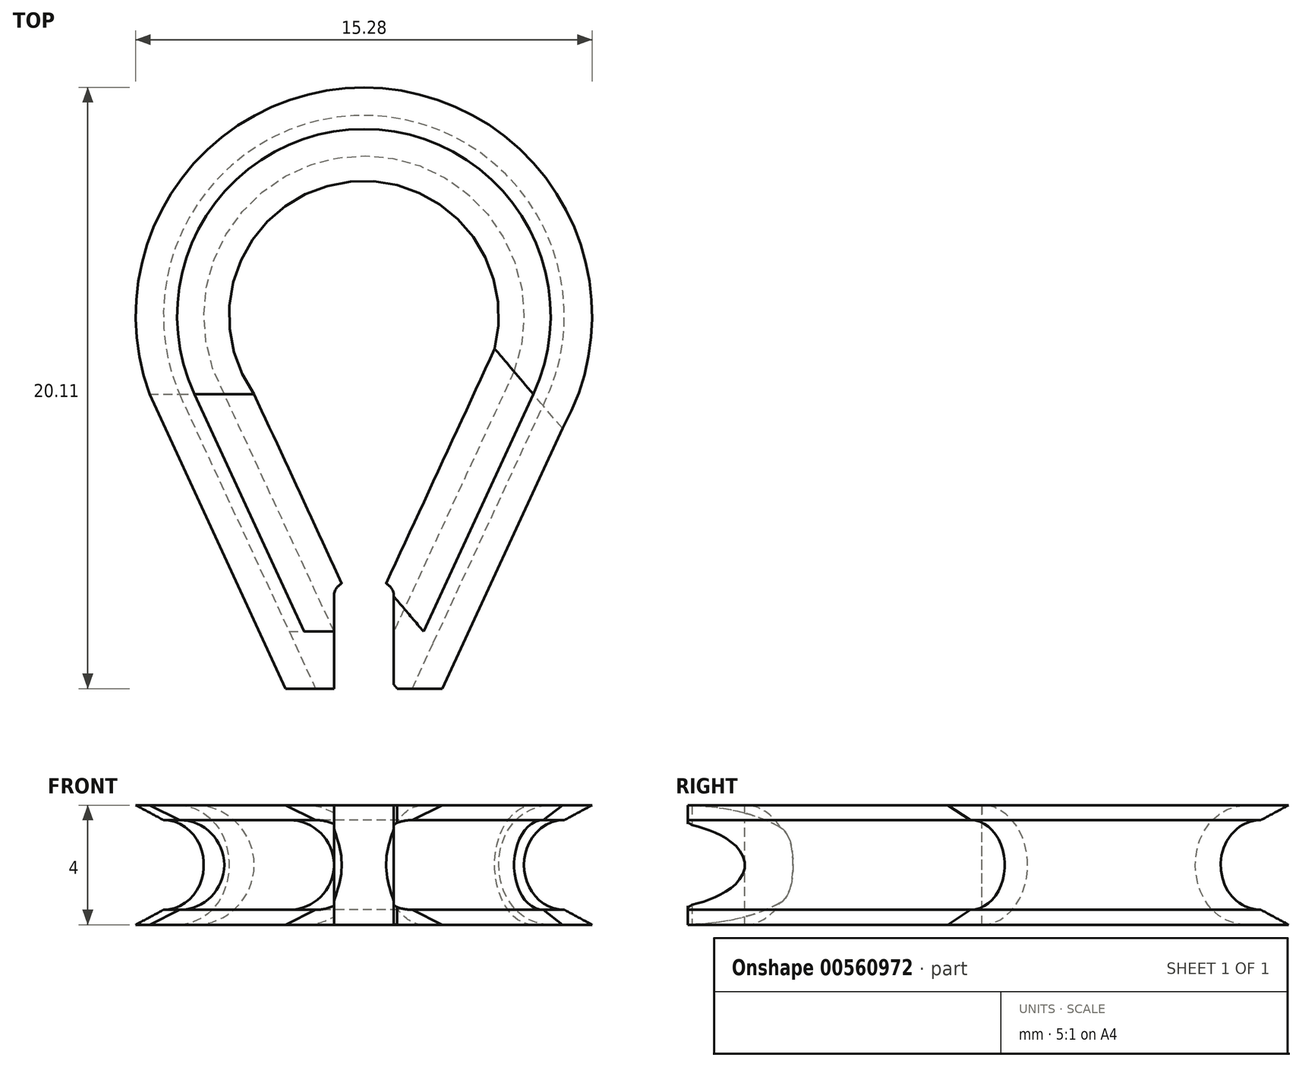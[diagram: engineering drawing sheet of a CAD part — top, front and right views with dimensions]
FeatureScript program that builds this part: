
annotation { "Feature Type Name" : "Feature", "Feature Type Description" : "" }
export const myFeature = defineFeature(function(context is Context, id is Id, definition is map)
    precondition{}
    {
        {
            var Q0;
            Q0=qCreatedBy(makeId("Top.planeOp"),FACE);
            var sketch = newSketch(context, id + "F0", { "sketchPlane" : qUnion([Q0])});
            skArc(sketch, "E0", {"start": v(5.67, -2.62) * mm, "mid": v(0, 6.25) * mm, "end": v(-5.67, -2.62) * mm});
            skLineSegment(sketch, "E1", {"start": v(-5.67, -2.62) * mm, "end": v(-2, -10.56) * mm});
            skLineSegment(sketch, "E2", {"start": v(5.67, -2.62) * mm, "end": v(2, -10.56) * mm});
            skLineSegment(sketch, "E3", {"start": v(2, -10.56) * mm, "end": v(1.12, -12.47) * mm});
            skLineSegment(sketch, "E4", {"start": v(-2, -10.56) * mm, "end": v(-1.12, -12.47) * mm});
            skSolve(sketch);
        }
        {
            var Q0;
            Q0=qCreatedBy(makeId("Front.planeOp"),FACE);
            cPlane(context, id + "F1", {"entities" : qUnion([Q0]), "cplaneType" : CPlaneType.OFFSET, "offset" : 10.56 * mm, "width" : 150 * mm, "height" : 150 * mm});
        }
        {
            var Q0;
            Q0=qCreatedBy(id+"F1.planeOp",FACE);
            var sketch = newSketch(context, id + "F2", { "sketchPlane" : qUnion([Q0])});
            skArc(sketch, "E5", {"start": v(-2, -2) * mm, "mid": v(0, 0) * mm, "end": v(-2, 2) * mm});
            skLineSegment(sketch, "E6", {"start": v(-2, 2) * mm, "end": v(-3.5, 2) * mm});
            skLineSegment(sketch, "E7", {"start": v(-2, -2) * mm, "end": v(-3.5, -2) * mm});
            skArc(sketch, "E8", {"start": v(-2.5, -1.5) * mm, "mid": v(-1, 0) * mm, "end": v(-2.5, 1.5) * mm});
            skLineSegment(sketch, "E9", {"start": v(-3.5, -2) * mm, "end": v(-2.5, -1.5) * mm});
            skLineSegment(sketch, "E10", {"start": v(-3.5, 2) * mm, "end": v(-2.5, 1.5) * mm});
            skSolve(sketch);
        }
        {
            var Q0;
            Q0=makeQuery(id+"F2.imprint","IMPRINT",FACE,{"disambiguationData":[TD([[makeQuery(id+"F2.imprint","IMPRINT",EDGE,{"derivedFrom":sQuery(id+"F2.wireOp",EDGE,"E5")}),1.0]])]});
            var Q1;
            Q1=sQuery(id+"F0.wireOp",EDGE,"E1");
            var Q2;
            Q2=sQuery(id+"F0.wireOp",EDGE,"E0");
            var Q3;
            Q3=sQuery(id+"F0.wireOp",EDGE,"E2");
            var Q4;
            Q4=sQuery(id+"F0.wireOp",EDGE,"E3");
            var Q5;
            Q5=sQuery(id+"F0.wireOp",EDGE,"GWWCwwxk-2lKG-hGvJ-B77L-LlExM1dhrJZM");
            var Q6;
            Q6=sQuery(id+"F0.wireOp",EDGE,"E4");
            sweep(context, id + "F3", {"profiles" : qUnion([Q0]), "path" : qUnion([Q1, Q2, Q3, Q4, Q5, Q6])});
        }
        {
            var Q0;
            Q0=qCreatedBy(makeId("Right.planeOp"),FACE);
            var sketch = newSketch(context, id + "F4", { "sketchPlane" : qUnion([Q0])});
            skLineSegment(sketch, "E11.bottom", {"start": v(-8.9, 3.55) * mm, "end": v(-22.25, 3.55) * mm});
            skLineSegment(sketch, "E11.top", {"start": v(-8.9, -3.55) * mm, "end": v(-22.25, -3.55) * mm});
            skLineSegment(sketch, "E11.left", {"start": v(-8.9, 3.55) * mm, "end": v(-8.9, -3.55) * mm});
            skLineSegment(sketch, "E11.right", {"start": v(-22.25, 3.55) * mm, "end": v(-22.25, -3.55) * mm});
            skPoint(sketch, "E11.middle", {"position": v(-15.57, 0) * mm});
            skSolve(sketch);
        }
        {
            var Q0;
            Q0=makeQuery(id+"F4.imprint","IMPRINT",FACE,{"disambiguationData":[TD([[makeQuery(id+"F4.imprint","IMPRINT",EDGE,{"derivedFrom":sQuery(id+"F4.wireOp",EDGE,"E11.bottom")}),1.0]])]});
            extrude(context, id + "F5", {"entities" : qUnion([Q0]), "operationType" : NewBodyOperationType.REMOVE, "oppositeDirection" : true, "depth" : 2 * mm, "offsetDistance" : 25 * mm, "symmetric" : true});
        }
        {
            var Q0;
            Q0=makeQuery(id+"F5.boolean.opBoolean","COPY",EDGE,{"derivedFrom":makeQuery(id+"F5.opExtrude","CAP_EDGE",EDGE,{"disambiguationData":[OSD([sQuery(id+"F4.wireOp",EDGE,"E11.left")])],"isStart":false})});
            var Q1;
            Q1=makeQuery(id+"F5.boolean.opBoolean","COPY",EDGE,{"derivedFrom":makeQuery(id+"F5.opExtrude","CAP_EDGE",EDGE,{"disambiguationData":[OSD([sQuery(id+"F4.wireOp",EDGE,"E11.left")])],"isStart":true})});
            fillet(context, id + "F6", {"entities" : qUnion([Q0, Q1]), "radius" : 0.5 * mm, "tangentPropagation" : true, "allowEdgeOverflow" : false});
        }
        {
            var Q0;
            {var subQ0=sQuery(id+"F2.wireOp",EDGE,"E8");var subQ2=sQuery(id+"F2.wireOp",EDGE,"E9");var subQ3=sQuery(id+"F2.wireOp",EDGE,"E7");var subQ4=sQuery(id+"F2.wireOp",EDGE,"E5");Q0=makeQuery(id+"F5.boolean.opBoolean","SPLIT",FACE,{"disambiguationData":[TD([makeQuery(id+"F3.opSweep","SWEPT_FACE",FACE,{"disambiguationData":[OSD([sQuery(id+"F0.wireOp",EDGE,"E1"),subQ2])]})])],"derivedFrom":makeQuery(id+"F3.opSweep","CAP_FACE",FACE,{"disambiguationData":[OSD([sQuery(id+"F0.wireOp",VERTEX,"E4.end"),subQ4,sQuery(id+"F2.wireOp",EDGE,"E6"),subQ3,subQ0,subQ2,sQuery(id+"F2.wireOp",EDGE,"E10")])],"isStart":false})});}
            var sketch = newSketch(context, id + "F7", { "sketchPlane" : qUnion([Q0])});
            skLineSegment(sketch, "E12.bottom", {"start": v(0, 2.87) * mm, "end": v(4.54, 2.87) * mm});
            skLineSegment(sketch, "E12.top", {"start": v(0, -3.31) * mm, "end": v(4.54, -3.31) * mm});
            skLineSegment(sketch, "E12.left", {"start": v(0, 2.87) * mm, "end": v(0, -3.31) * mm});
            skLineSegment(sketch, "E12.right", {"start": v(4.54, 2.87) * mm, "end": v(4.54, -3.31) * mm});
            skSolve(sketch);
        }
        {
            var Q0;
            Q0 = qSketchRegion(id + "F7", true);
            extrude(context, id + "F8", {"entities" : qUnion([Q0]), "operationType" : NewBodyOperationType.REMOVE, "endBound" : BoundingType.THROUGH_ALL, "depth" : 25 * mm, "offsetDistance" : 25 * mm});
        }
    });
